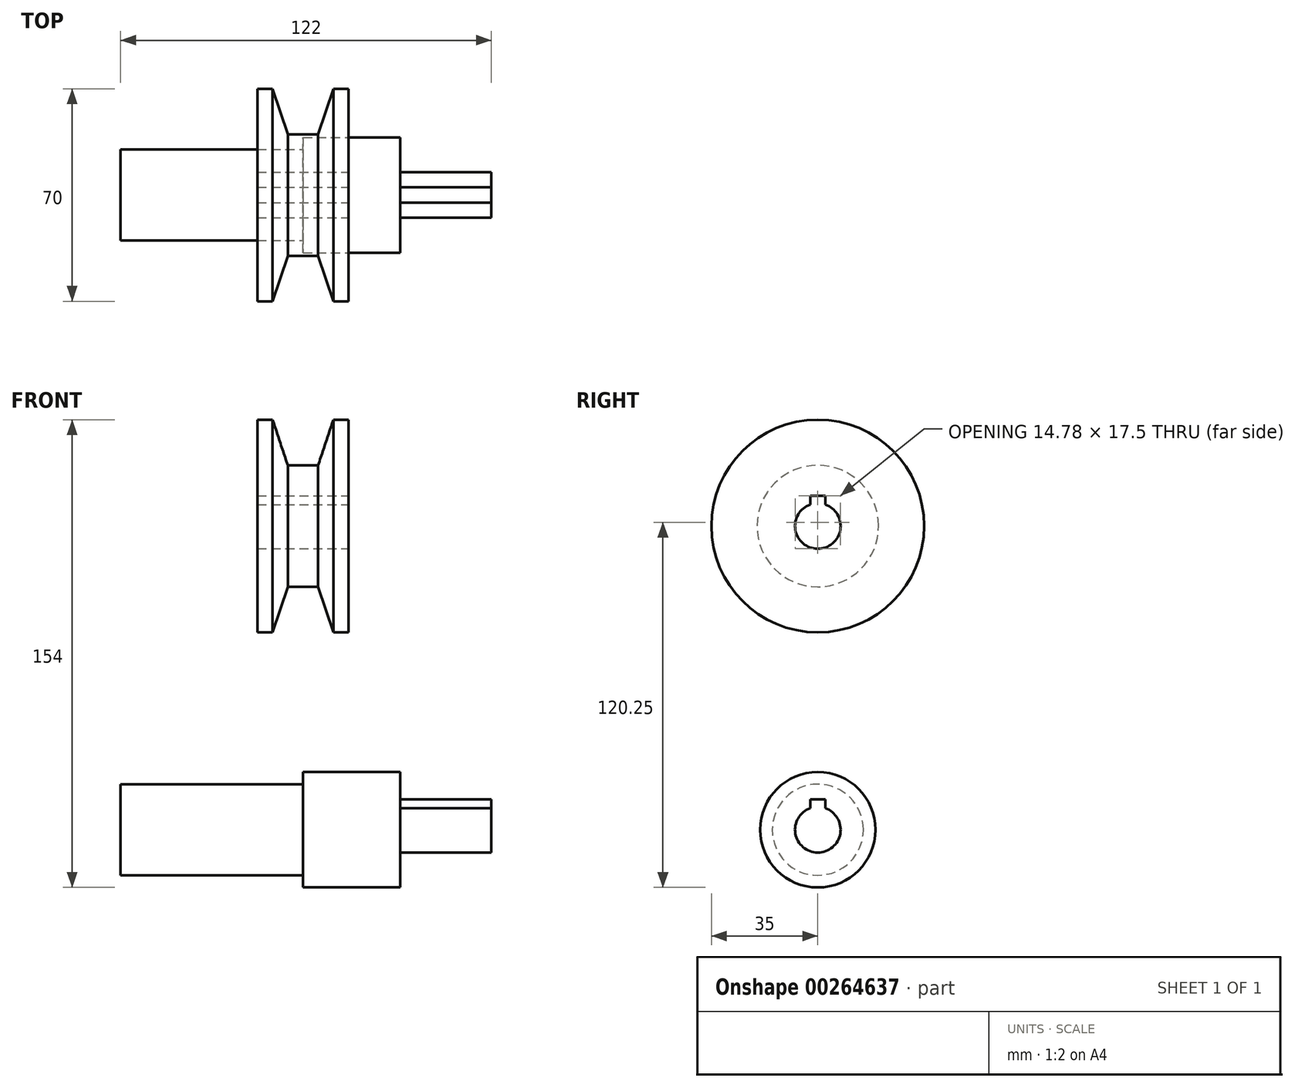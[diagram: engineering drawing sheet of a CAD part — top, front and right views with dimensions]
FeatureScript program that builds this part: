
annotation { "Feature Type Name" : "Feature", "Feature Type Description" : "" }
export const myFeature = defineFeature(function(context is Context, id is Id, definition is map)
    precondition{}
    {
        {
            var Q0;
            Q0=qCreatedBy(makeId("Front.planeOp"),FACE);
            var sketch = newSketch(context, id + "F0", { "sketchPlane" : qUnion([Q0])});
            skLineSegment(sketch, "E0", {"start": v(-60, 0) * mm, "end": v(-60, 15) * mm});
            skLineSegment(sketch, "E1", {"start": v(-60, 15) * mm, "end": v(0, 15) * mm});
            skLineSegment(sketch, "E2", {"start": v(0, 15) * mm, "end": v(0, 19) * mm});
            skLineSegment(sketch, "E3", {"start": v(0, 19) * mm, "end": v(32, 19) * mm});
            skLineSegment(sketch, "E4", {"start": v(32, 19) * mm, "end": v(32, 7.5) * mm});
            skLineSegment(sketch, "E5", {"start": v(32, 7.5) * mm, "end": v(62, 7.5) * mm});
            skLineSegment(sketch, "E6", {"start": v(62, 7.5) * mm, "end": v(62, 0) * mm});
            skLineSegment(sketch, "E7", {"start": v(62, 0) * mm, "end": v(0, 0) * mm});
            skLineSegment(sketch, "E8", {"start": v(0, 0) * mm, "end": v(-60, 0) * mm});
            skLineSegment(sketch, "E9", {"start": v(-15, 135) * mm, "end": v(-10, 135) * mm});
            skLineSegment(sketch, "E10", {"start": v(-10, 135) * mm, "end": v(-5, 120) * mm});
            skLineSegment(sketch, "E11", {"start": v(-5, 120) * mm, "end": v(5, 120) * mm});
            skLineSegment(sketch, "E12", {"start": v(5, 120) * mm, "end": v(10, 135) * mm});
            skLineSegment(sketch, "E13", {"start": v(10, 135) * mm, "end": v(15, 135) * mm});
            skLineSegment(sketch, "E14", {"start": v(15, 135) * mm, "end": v(15, 100) * mm});
            skLineSegment(sketch, "E15", {"start": v(15, 100) * mm, "end": v(15, 65) * mm});
            skLineSegment(sketch, "E16", {"start": v(15, 65) * mm, "end": v(10, 65) * mm});
            skLineSegment(sketch, "E17", {"start": v(10, 65) * mm, "end": v(5, 80) * mm});
            skLineSegment(sketch, "E18", {"start": v(5, 80) * mm, "end": v(0, 80) * mm});
            skLineSegment(sketch, "E19", {"start": v(0, 80) * mm, "end": v(-5, 80) * mm});
            skLineSegment(sketch, "E20", {"start": v(-5, 80) * mm, "end": v(-10, 65) * mm});
            skLineSegment(sketch, "E21", {"start": v(-10, 65) * mm, "end": v(-15, 65) * mm});
            skLineSegment(sketch, "E22", {"start": v(-15, 65) * mm, "end": v(-15, 100) * mm});
            skLineSegment(sketch, "E23", {"start": v(-15, 100) * mm, "end": v(-15, 135) * mm});
            skLineSegment(sketch, "E24", {"start": v(-15, 100) * mm, "end": v(15, 100) * mm});
            skSolve(sketch);
        }
        {
            var Q0;
            Q0=qCreatedBy(makeId("Front.planeOp"),FACE);
            var sketch = newSketch(context, id + "F1", { "sketchPlane" : qUnion([Q0])});
            skLineSegment(sketch, "E25", {"start": v(0, 0) * mm, "end": v(0, 10) * mm});
            skLineSegment(sketch, "E26", {"start": v(0, 10) * mm, "end": v(62, 10) * mm});
            skLineSegment(sketch, "E27", {"start": v(62, 10) * mm, "end": v(62, 0) * mm});
            skLineSegment(sketch, "E28", {"start": v(62, 0) * mm, "end": v(0, 0) * mm});
            skSolve(sketch);
        }
        {
            var Q0;
            Q0=makeQuery(id+"F0.imprint","IMPRINT",FACE,{"disambiguationData":[TD([[makeQuery(id+"F0.imprint","IMPRINT",EDGE,{"derivedFrom":sQuery(id+"F0.wireOp",EDGE,"E0")}),-1.0]])]});
            var Q1;
            Q1=sQuery(id+"F0.wireOp",EDGE,"E8");
            revolve(context, id + "F2", {"entities" : qUnion([Q0]), "axis" : qUnion([Q1]), "revolveType" : RevolveType.FULL});
        }
        {
            var Q0;
            Q0=makeQuery(id+"F1.imprint","IMPRINT",FACE,{"disambiguationData":[TD([[makeQuery(id+"F1.imprint","IMPRINT",EDGE,{"derivedFrom":sQuery(id+"F1.wireOp",EDGE,"E25")}),-1.0]])]});
            extrude(context, id + "F3", {"entities" : qUnion([Q0]), "operationType" : NewBodyOperationType.ADD, "endBound" : BoundingType.SYMMETRIC, "depth" : 5 * mm});
        }
        {
            var Q0;
            Q0=makeQuery(id+"F0.imprint","IMPRINT",FACE,{"disambiguationData":[TD([[makeQuery(id+"F0.imprint","IMPRINT",EDGE,{"derivedFrom":sQuery(id+"F0.wireOp",EDGE,"E9")}),-1.0]])]});
            var Q1;
            Q1=sQuery(id+"F0.wireOp",EDGE,"E24");
            revolve(context, id + "F4", {"entities" : qUnion([Q0]), "axis" : qUnion([Q1]), "revolveType" : RevolveType.FULL});
        }
        {
            var Q0;
            Q0=qCreatedBy(makeId("Right.planeOp"),FACE);
            var sketch = newSketch(context, id + "F5", { "sketchPlane" : qUnion([Q0])});
            skCircle(sketch, "E29", {"center": v(0, 100) * mm, "radius": 7.5 * mm});
            skLineSegment(sketch, "E30", {"start": v(-2.5, 107.07) * mm, "end": v(-2.5, 110) * mm});
            skLineSegment(sketch, "E31", {"start": v(-2.5, 110) * mm, "end": v(2.5, 110) * mm});
            skLineSegment(sketch, "E32", {"start": v(2.5, 110) * mm, "end": v(2.5, 107.07) * mm});
            skSolve(sketch);
        }
        {
            var Q0;
            Q0 = qSketchRegion(id + "F5", true);
            extrude(context, id + "F6", {"entities" : qUnion([Q0]), "operationType" : NewBodyOperationType.REMOVE, "endBound" : BoundingType.SYMMETRIC, "oppositeDirection" : true, "depth" : 30 * mm});
        }
    });
